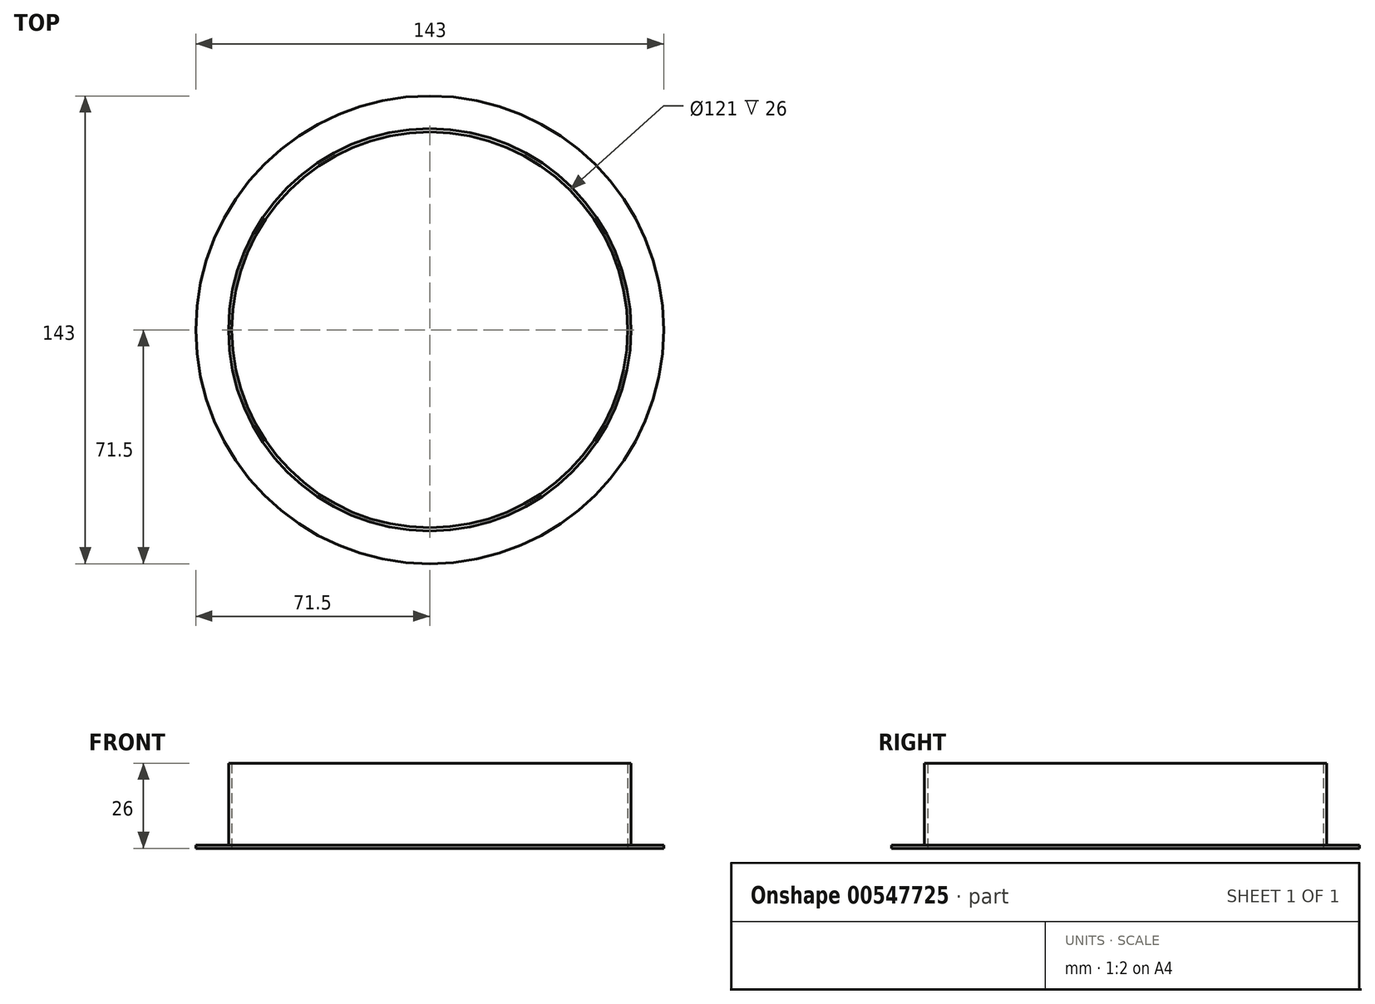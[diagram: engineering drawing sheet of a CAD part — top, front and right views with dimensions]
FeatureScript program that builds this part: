
annotation { "Feature Type Name" : "Feature", "Feature Type Description" : "" }
export const myFeature = defineFeature(function(context is Context, id is Id, definition is map)
    precondition{}
    {
        {
            var Q0;
            Q0=qCreatedBy(makeId("Front.planeOp"),FACE);
            var sketch = newSketch(context, id + "F0", { "sketchPlane" : qUnion([Q0])});
            skLineSegment(sketch, "E0", {"start": v(0, 0) * mm, "end": v(0, 50.15) * mm, "construction": true});
            skLineSegment(sketch, "E1", {"start": v(-71.5, 0) * mm, "end": v(-71.5, 1) * mm});
            skLineSegment(sketch, "E2", {"start": v(-71.5, 1) * mm, "end": v(-61.5, 1) * mm});
            skLineSegment(sketch, "E3", {"start": v(-61.5, 1) * mm, "end": v(-61.5, 26) * mm});
            skLineSegment(sketch, "E4", {"start": v(-61.5, 26) * mm, "end": v(-60.5, 26) * mm});
            skLineSegment(sketch, "E5", {"start": v(-60.5, 26) * mm, "end": v(-60.5, 0) * mm});
            skLineSegment(sketch, "E6", {"start": v(-60.5, 0) * mm, "end": v(-71.5, 0) * mm});
            skSolve(sketch);
        }
        {
            var Q0;
            Q0=qSketchRegion(id+"F0",true);
            var Q1;
            Q1=sQuery(id+"F0.wireOp",EDGE,"E0");
            revolve(context, id + "F1", {"surfaceOperationType" : NewSurfaceOperationType.NEW, "entities" : qUnion([Q0]), "axis" : qUnion([Q1]), "revolveType" : RevolveType.FULL});
        }
    });
